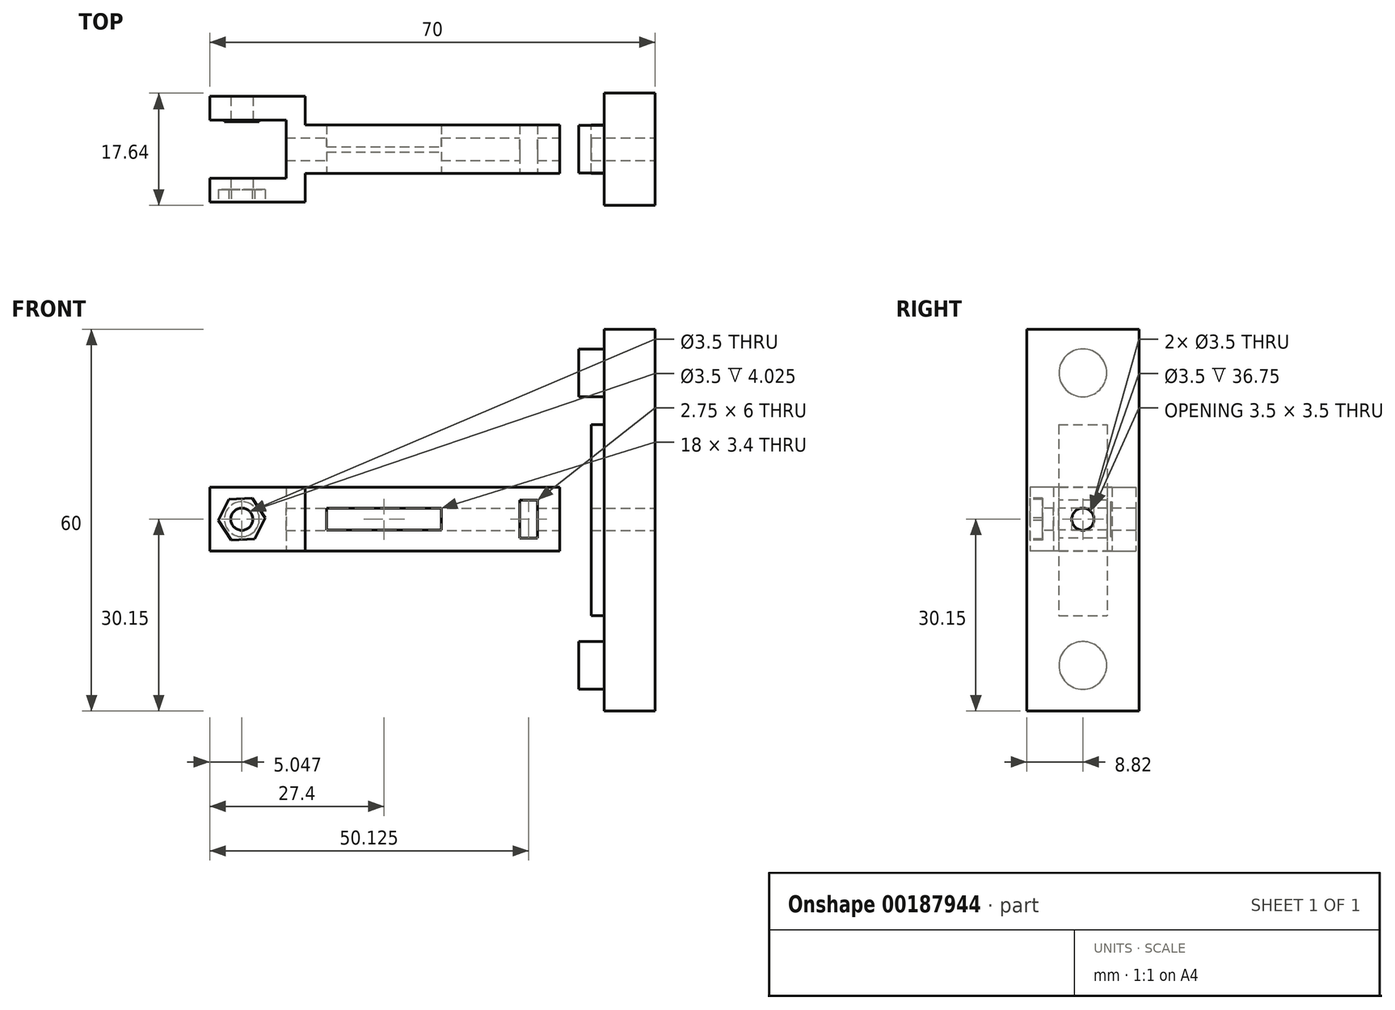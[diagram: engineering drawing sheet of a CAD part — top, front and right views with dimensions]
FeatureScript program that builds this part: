
annotation { "Feature Type Name" : "Feature", "Feature Type Description" : "" }
export const myFeature = defineFeature(function(context is Context, id is Id, definition is map)
    precondition{}
    {
        {
            var Q0;
            Q0=qCreatedBy(makeId("Top.planeOp"),FACE);
            var sketch = newSketch(context, id + "F0", { "sketchPlane" : qUnion([Q0])});
            skLineSegment(sketch, "E0.bottom", {"start": v(0, 0) * mm, "end": v(40, 0) * mm});
            skLineSegment(sketch, "E0.top", {"start": v(0, -3.83) * mm, "end": v(40, -3.83) * mm});
            skLineSegment(sketch, "E0.left", {"start": v(0, 0) * mm, "end": v(0, -3.83) * mm});
            skLineSegment(sketch, "E0.right", {"start": v(40, 0) * mm, "end": v(40, -3.83) * mm});
            skLineSegment(sketch, "E1.bottom", {"start": v(-3, 0) * mm, "end": v(0, 0) * mm});
            skLineSegment(sketch, "E1.top", {"start": v(-15, -8.32) * mm, "end": v(0, -8.32) * mm});
            skLineSegment(sketch, "E1.left", {"start": v(-15, -4.6) * mm, "end": v(-15, -8.32) * mm});
            skLineSegment(sketch, "E1.right", {"start": v(0, 0) * mm, "end": v(0, -8.32) * mm});
            skLineSegment(sketch, "E2.top", {"start": v(-15, -4.6) * mm, "end": v(-3, -4.6) * mm});
            skLineSegment(sketch, "E2.right", {"start": v(-3, 0) * mm, "end": v(-3, -4.6) * mm});
            skLineSegment(sketch, "E3.MirrorCS", {"start": v(0, 0) * mm, "end": v(0, 3.83) * mm});
            skLineSegment(sketch, "E4.MirrorCS", {"start": v(0, 0) * mm, "end": v(0, 8.32) * mm});
            skLineSegment(sketch, "E5.MirrorCS", {"start": v(-15, 4.6) * mm, "end": v(-15, 8.32) * mm});
            skLineSegment(sketch, "E6.MirrorCS", {"start": v(-3, 0) * mm, "end": v(-3, 4.6) * mm});
            skLineSegment(sketch, "E7.MirrorCS", {"start": v(-15, 8.32) * mm, "end": v(0, 8.32) * mm});
            skLineSegment(sketch, "E8.MirrorCS", {"start": v(-15, 4.6) * mm, "end": v(-3, 4.6) * mm});
            skLineSegment(sketch, "E9.MirrorCS", {"start": v(40, 0) * mm, "end": v(40, 3.83) * mm});
            skLineSegment(sketch, "E10.MirrorCS", {"start": v(0, 3.83) * mm, "end": v(40, 3.83) * mm});
            skSolve(sketch);
        }
        {
            var Q0;
            {var subQ2=sQuery(id+"F0.wireOp",EDGE,"E1.top");Q0=makeQuery(id+"F0.imprint","IMPRINT",FACE,{"disambiguationData":[TD([[makeQuery(id+"F0.imprint","IMPRINT",EDGE,{"derivedFrom":subQ2}),1.0]])]});}
            var Q1;
            Q1=makeQuery(id+"F0.imprint","IMPRINT",FACE,{"disambiguationData":[TD([[makeQuery(id+"F0.imprint","IMPRINT",EDGE,{"derivedFrom":sQuery(id+"F0.wireOp",EDGE,"E5.MirrorCS")}),-1.0]])]});
            var Q2;
            {var subQ0=sQuery(id+"F0.wireOp",EDGE,"E0.bottom");Q2=makeQuery(id+"F0.imprint","IMPRINT",FACE,{"disambiguationData":[TD([[makeQuery(id+"F0.imprint","IMPRINT",EDGE,{"derivedFrom":subQ0}),1.0]])]});}
            var Q3;
            {var subQ0=sQuery(id+"F0.wireOp",EDGE,"E0.bottom");Q3=makeQuery(id+"F0.imprint","IMPRINT",FACE,{"disambiguationData":[TD([[makeQuery(id+"F0.imprint","IMPRINT",EDGE,{"derivedFrom":subQ0}),-1.0]])]});}
            extrude(context, id + "F1", {"entities" : qUnion([Q0, Q1, Q2, Q3]), "depth" : 10 * mm});
        }
        {
            var Q0;
            Q0=makeQuery(id+"F1.opExtrude","SWEPT_FACE",FACE,{"disambiguationData":[OSD([sQuery(id+"F0.wireOp",EDGE,"E1.top")])]});
            var sketch = newSketch(context, id + "F2", { "sketchPlane" : qUnion([Q0])});
            skCircle(sketch, "E11", {"center": v(-9.95, 5) * mm, "radius": 1.75 * mm});
            skSolve(sketch);
        }
        {
            var Q0;
            Q0=makeQuery(id+"F2.imprint","IMPRINT",FACE,{"disambiguationData":[TD([[makeQuery(id+"F2.imprint","IMPRINT",EDGE,{"derivedFrom":sQuery(id+"F2.wireOp",EDGE,"E11")}),1.0]])]});
            extrude(context, id + "F3", {"entities" : qUnion([Q0]), "operationType" : NewBodyOperationType.REMOVE, "endBound" : BoundingType.THROUGH_ALL, "oppositeDirection" : true, "depth" : 25 * mm});
        }
        {
            var Q0;
            Q0=makeQuery(id+"F1.opExtrude","SWEPT_FACE",FACE,{"disambiguationData":[OSD([sQuery(id+"F0.wireOp",EDGE,"E0.top")])]});
            var sketch = newSketch(context, id + "F4", { "sketchPlane" : qUnion([Q0])});
            skLineSegment(sketch, "E12.bottom", {"start": v(3.4, 3.3) * mm, "end": v(21.4, 3.3) * mm});
            skLineSegment(sketch, "E12.top", {"start": v(3.4, 6.7) * mm, "end": v(21.4, 6.7) * mm});
            skLineSegment(sketch, "E12.left", {"start": v(3.4, 3.3) * mm, "end": v(3.4, 6.7) * mm});
            skLineSegment(sketch, "E12.right", {"start": v(21.4, 3.3) * mm, "end": v(21.4, 6.7) * mm});
            skLineSegment(sketch, "E13.bottom", {"start": v(33.75, 8) * mm, "end": v(36.5, 8) * mm});
            skLineSegment(sketch, "E13.top", {"start": v(33.75, 2) * mm, "end": v(36.5, 2) * mm});
            skLineSegment(sketch, "E13.left", {"start": v(33.75, 8) * mm, "end": v(33.75, 2) * mm});
            skLineSegment(sketch, "E13.right", {"start": v(36.5, 8) * mm, "end": v(36.5, 2) * mm});
            skSolve(sketch);
        }
        {
            var Q0;
            Q0=makeQuery(id+"F4.imprint","IMPRINT",FACE,{"disambiguationData":[TD([[makeQuery(id+"F4.imprint","IMPRINT",EDGE,{"derivedFrom":sQuery(id+"F4.wireOp",EDGE,"E12.bottom")}),1.0]])]});
            var Q1;
            Q1=makeQuery(id+"F4.imprint","IMPRINT",FACE,{"disambiguationData":[TD([[makeQuery(id+"F4.imprint","IMPRINT",EDGE,{"derivedFrom":sQuery(id+"F4.wireOp",EDGE,"E13.bottom")}),-1.0]])]});
            extrude(context, id + "F5", {"entities" : qUnion([Q0, Q1]), "operationType" : NewBodyOperationType.REMOVE, "endBound" : BoundingType.THROUGH_ALL, "oppositeDirection" : true, "depth" : 25 * mm});
        }
        {
            var Q0;
            Q0=makeQuery(id+"F1.opExtrude","SWEPT_FACE",FACE,{"disambiguationData":[OSD([sQuery(id+"F0.wireOp",EDGE,"E0.right"),sQuery(id+"F0.wireOp",EDGE,"E9.MirrorCS")])]});
            var sketch = newSketch(context, id + "F6", { "sketchPlane" : qUnion([Q0])});
            skCircle(sketch, "E14", {"center": v(0, 5) * mm, "radius": 1.75 * mm});
            skSolve(sketch);
        }
        {
            var Q0;
            Q0=makeQuery(id+"F6.imprint","IMPRINT",FACE,{"disambiguationData":[TD([[makeQuery(id+"F6.imprint","IMPRINT",EDGE,{"derivedFrom":sQuery(id+"F6.wireOp",EDGE,"E14")}),1.0]])]});
            extrude(context, id + "F7", {"entities" : qUnion([Q0]), "operationType" : NewBodyOperationType.REMOVE, "oppositeDirection" : true, "depth" : 15 * mm});
        }
        {
            var Q0;
            Q0=makeQuery(id+"F1.opExtrude","SWEPT_FACE",FACE,{"disambiguationData":[OSD([sQuery(id+"F0.wireOp",EDGE,"E0.right"),sQuery(id+"F0.wireOp",EDGE,"E9.MirrorCS")])]});
            cPlane(context, id + "F8", {"entities" : qUnion([Q0]), "cplaneType" : CPlaneType.OFFSET, "offset" : 5 * mm, "width" : 150 * mm, "height" : 150 * mm});
        }
        {
            var Q0;
            Q0=qCreatedBy(id+"F8.planeOp",FACE);
            var sketch = newSketch(context, id + "F9", { "sketchPlane" : qUnion([Q0])});
            skLineSegment(sketch, "E15.0", {"start": v(3.83, 10) * mm, "end": v(3.83, 0) * mm});
            skLineSegment(sketch, "E16.0", {"start": v(-3.82, 10) * mm, "end": v(-3.82, 0) * mm});
            skLineSegment(sketch, "E17.bottom", {"start": v(-3.82, 19.85) * mm, "end": v(3.83, 19.85) * mm});
            skLineSegment(sketch, "E17.top", {"start": v(-3.82, -10.15) * mm, "end": v(3.83, -10.15) * mm});
            skLineSegment(sketch, "E17.left", {"start": v(-3.82, 19.85) * mm, "end": v(-3.82, -10.15) * mm});
            skLineSegment(sketch, "E17.right", {"start": v(3.83, 19.85) * mm, "end": v(3.83, -10.15) * mm});
            skPoint(sketch, "E18.oppositeSnap0", {"position": v(3.83, 4.85) * mm});
            skLineSegment(sketch, "E18.bottom", {"start": v(3.83, 4.85) * mm, "end": v(3.83, 4.85) * mm});
            skLineSegment(sketch, "E18.top", {"start": v(3.83, 4.85) * mm, "end": v(3.83, 4.85) * mm});
            skLineSegment(sketch, "E18.left", {"start": v(3.83, 4.85) * mm, "end": v(3.83, 4.85) * mm});
            skLineSegment(sketch, "E18.right", {"start": v(3.83, 4.85) * mm, "end": v(3.83, 4.85) * mm});
            skSolve(sketch);
        }
        {
            var Q0;
            {var subQ0=sQuery(id+"F9.wireOp",EDGE,"E17.bottom");Q0=makeQuery(id+"F9.imprint","IMPRINT",FACE,{"disambiguationData":[TD([[makeQuery(id+"F9.imprint","IMPRINT",EDGE,{"derivedFrom":subQ0}),-1.0]])]});}
            extrude(context, id + "F10", {"entities" : qUnion([Q0]), "depth" : 2 * mm});
        }
        {
            var Q0;
            Q0=makeQuery(id+"F10.opExtrude","CAP_FACE",FACE,{"disambiguationData":[OSD([sQuery(id+"F9.wireOp",EDGE,"E17.bottom"),sQuery(id+"F9.wireOp",EDGE,"E17.top"),sQuery(id+"F9.wireOp",EDGE,"E17.left"),sQuery(id+"F9.wireOp",EDGE,"E17.right")])],"isStart":false});
            var sketch = newSketch(context, id + "F11", { "sketchPlane" : qUnion([Q0])});
            skLineSegment(sketch, "E19.bottom", {"start": v(8.82, 34.85) * mm, "end": v(-8.83, 34.85) * mm});
            skLineSegment(sketch, "E19.top", {"start": v(8.83, -25.15) * mm, "end": v(-8.82, -25.15) * mm});
            skLineSegment(sketch, "E19.left", {"start": v(8.82, 34.85) * mm, "end": v(8.83, -25.15) * mm});
            skLineSegment(sketch, "E19.right", {"start": v(-8.83, 34.85) * mm, "end": v(-8.82, -25.15) * mm});
            skSolve(sketch);
        }
        {
            var Q0;
            Q0 = qSketchRegion(id + "F11", true);
            extrude(context, id + "F12", {"entities" : qUnion([Q0]), "operationType" : NewBodyOperationType.ADD, "depth" : 8 * mm});
        }
        {
            var Q0;
            Q0=makeQuery(id+"F12.opExtrude","CAP_FACE",FACE,{"disambiguationData":[OSD([sQuery(id+"F11.wireOp",EDGE,"E19.bottom"),sQuery(id+"F11.wireOp",EDGE,"E19.top"),sQuery(id+"F11.wireOp",EDGE,"E19.left"),sQuery(id+"F11.wireOp",EDGE,"E19.right")])],"isStart":false});
            var sketch = newSketch(context, id + "F13", { "sketchPlane" : qUnion([Q0])});
            skCircle(sketch, "E20.0", {"center": v(0, 5) * mm, "radius": 1.75 * mm});
            skSolve(sketch);
        }
        {
            var Q0;
            Q0=makeQuery(id+"F13.imprint","IMPRINT",FACE,{"disambiguationData":[TD([[makeQuery(id+"F13.imprint","IMPRINT",EDGE,{"derivedFrom":sQuery(id+"F13.wireOp",EDGE,"E20.0")}),1.0]])]});
            extrude(context, id + "F14", {"entities" : qUnion([Q0]), "operationType" : NewBodyOperationType.REMOVE, "endBound" : BoundingType.THROUGH_ALL, "oppositeDirection" : true, "depth" : 25 * mm});
        }
        {
            var Q0;
            Q0=makeQuery(id+"F1.opExtrude","SWEPT_FACE",FACE,{"disambiguationData":[OSD([sQuery(id+"F0.wireOp",EDGE,"E8.MirrorCS")])]});
            var sketch = newSketch(context, id + "F15", { "sketchPlane" : qUnion([Q0])});
            skCircle(sketch, "E21", {"center": v(-9.95, 5) * mm, "radius": 1.75 * mm});
            skCircle(sketch, "E22", {"center": v(-9.95, 5) * mm, "radius": 2.75 * mm});
            skSolve(sketch);
        }
        {
            var Q0;
            Q0=makeQuery(id+"F15.imprint","IMPRINT",FACE,{"disambiguationData":[TD([[makeQuery(id+"F15.imprint","IMPRINT",EDGE,{"derivedFrom":sQuery(id+"F15.wireOp",EDGE,"E21")}),1.0]])]});
            extrude(context, id + "F16", {"entities" : qUnion([Q0]), "operationType" : NewBodyOperationType.ADD, "depth" : 0.3 * mm});
        }
        {
            var Q0;
            Q0=makeQuery(id+"F1.opExtrude","SWEPT_FACE",FACE,{"disambiguationData":[OSD([sQuery(id+"F0.wireOp",EDGE,"E1.top")])]});
            var sketch = newSketch(context, id + "F17", { "sketchPlane" : qUnion([Q0])});
            skCircle(sketch, "E23.cCircle", {"center": v(-9.95, 5) * mm, "radius": 3.2 * mm, "construction": true});
            skLineSegment(sketch, "E23.0", {"start": v(-6.26, 5.2) * mm, "end": v(-7.93, 1.9) * mm});
            skLineSegment(sketch, "E23.1", {"start": v(-7.93, 1.9) * mm, "end": v(-11.62, 1.7) * mm});
            skLineSegment(sketch, "E23.2", {"start": v(-11.62, 1.7) * mm, "end": v(-13.64, 4.8) * mm});
            skLineSegment(sketch, "E23.3", {"start": v(-13.64, 4.8) * mm, "end": v(-11.98, 8.1) * mm});
            skLineSegment(sketch, "E23.4", {"start": v(-11.98, 8.1) * mm, "end": v(-8.29, 8.3) * mm});
            skLineSegment(sketch, "E23.5", {"start": v(-8.29, 8.3) * mm, "end": v(-6.26, 5.2) * mm});
            skPoint(sketch, "E23.0.midPoint", {"position": v(-7.1, 3.56) * mm});
            skSolve(sketch);
        }
        {
            var Q0;
            Q0=makeQuery(id+"F17.imprint","IMPRINT",FACE,{"disambiguationData":[TD([[makeQuery(id+"F17.imprint","IMPRINT",EDGE,{"derivedFrom":sQuery(id+"F17.wireOp",EDGE,"E23.0")}),-1.0]])]});
            extrude(context, id + "F18", {"entities" : qUnion([Q0]), "operationType" : NewBodyOperationType.REMOVE, "oppositeDirection" : true, "depth" : 2 * mm});
        }
        {
            var Q0;
            Q0=makeQuery(id+"F12.opExtrude","CAP_FACE",FACE,{"disambiguationData":[OSD([sQuery(id+"F11.wireOp",EDGE,"E19.bottom"),sQuery(id+"F11.wireOp",EDGE,"E19.top"),sQuery(id+"F11.wireOp",EDGE,"E19.left"),sQuery(id+"F11.wireOp",EDGE,"E19.right")])],"isStart":true});
            var sketch = newSketch(context, id + "F19", { "sketchPlane" : qUnion([Q0])});
            skCircle(sketch, "E24.0", {"center": v(0, 5) * mm, "radius": 1.75 * mm});
            skCircle(sketch, "E25", {"center": v(0, -18) * mm, "radius": 3.75 * mm});
            skCircle(sketch, "E26", {"center": v(0, 28) * mm, "radius": 3.75 * mm});
            skSolve(sketch);
        }
        {
            var Q0;
            Q0=makeQuery(id+"F19.imprint","IMPRINT",FACE,{"disambiguationData":[TD([[makeQuery(id+"F19.imprint","IMPRINT",EDGE,{"derivedFrom":sQuery(id+"F19.wireOp",EDGE,"E26")}),1.0]])]});
            var Q1;
            Q1=makeQuery(id+"F19.imprint","IMPRINT",FACE,{"disambiguationData":[TD([[makeQuery(id+"F19.imprint","IMPRINT",EDGE,{"derivedFrom":sQuery(id+"F19.wireOp",EDGE,"E25")}),1.0]])]});
            extrude(context, id + "F20", {"entities" : qUnion([Q0, Q1]), "operationType" : NewBodyOperationType.ADD, "depth" : 4 * mm});
        }
    });
